# Revit family: 2630035-006 - CH Slop Hopper & 25mm Inlet Pipe
name_source: partatom
category: Plumbing Fixtures
units: mm (PartAtom-declared; Revit-internal decimal feet)

## family parameters
Always vertical = Yes
Cut with Voids When Loaded = No
OmniClass Number = 23.40.70.14.11
OmniClass Title = Hospitality Equipment and Furnishings
Part Type = Normal
Room Calculation Point = No
Round Connector Dimension = Use Diameter
Shared = No
Work Plane-Based = No

## types (1)
- CH Slop Hopper with 25mm Inlet Pipe
    Assembly Code = E1020
    CW Connection = Yes
    Default Elevation = 0 mm  [stored 0 ft]
    Dimensions = 540mm x 540mm x 415mm
    HW Connection = No
    Manufacturer = Franke South Africa (Pty) Ltd
    Material = Grade 304 18/10
    Model = CH Slop Hopper & 25mm Inlet Pipe
    Product Code = 2630035-006
    Vent Connection = No
    Waste Connection = Yes

note: [stored X ft] marks values corroborated as IEEE doubles in the binary element streams (Revit-internal decimal feet)

## geometry (parser evidence)
native form markers: Blend x14, Sweep x3
no freeform markers — native parametric forms only
